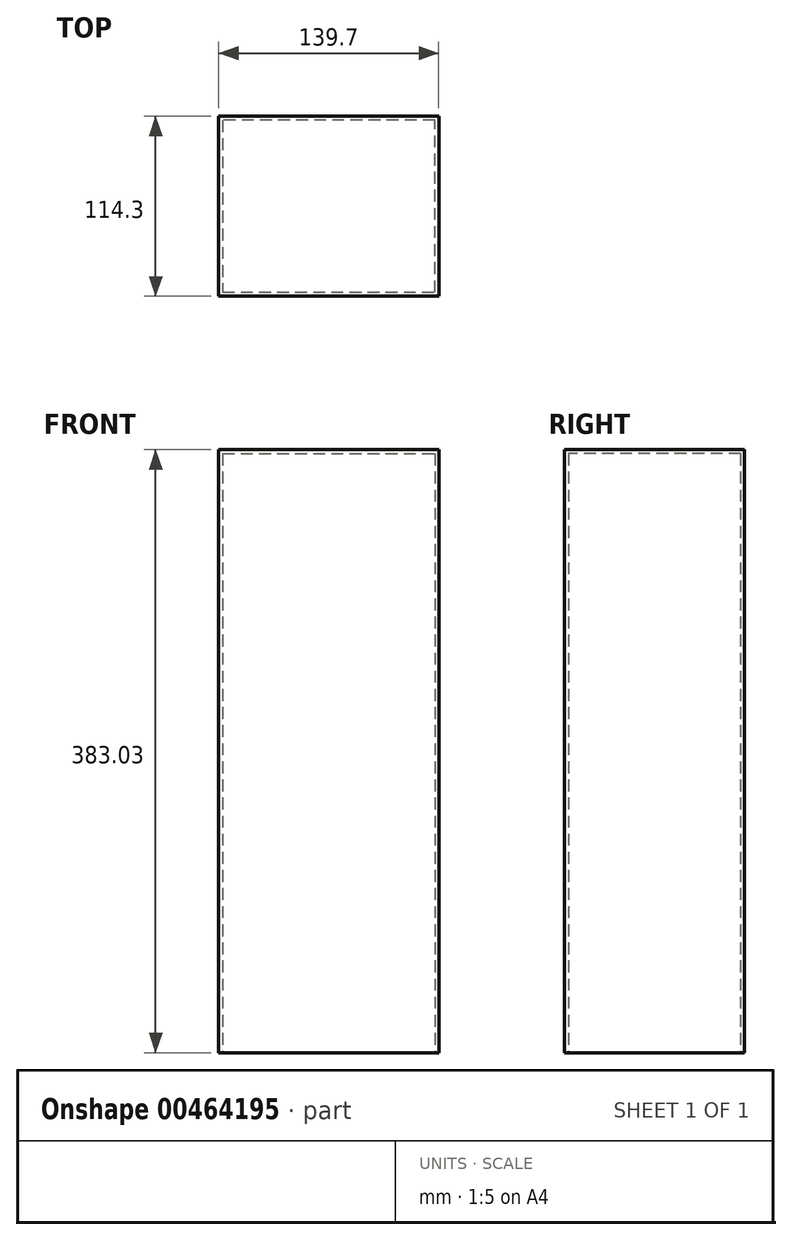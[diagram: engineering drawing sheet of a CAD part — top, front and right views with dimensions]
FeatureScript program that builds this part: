
annotation { "Feature Type Name" : "Feature", "Feature Type Description" : "" }
export const myFeature = defineFeature(function(context is Context, id is Id, definition is map)
    precondition{}
    {
        {
            var Q0;
            Q0=qCreatedBy(makeId("Top.planeOp"),FACE);
            var sketch = newSketch(context, id + "F0", { "sketchPlane" : qUnion([Q0])});
            skLineSegment(sketch, "E0", {"start": v(-63.05, -39.13) * mm, "end": v(76.65, -39.13) * mm});
            skLineSegment(sketch, "E1", {"start": v(76.65, -39.13) * mm, "end": v(76.65, 75.17) * mm});
            skLineSegment(sketch, "E2", {"start": v(76.65, 75.17) * mm, "end": v(-63.05, 75.17) * mm});
            skLineSegment(sketch, "E3", {"start": v(-63.05, 75.17) * mm, "end": v(-63.05, -39.13) * mm});
            skSolve(sketch);
        }
        {
            var Q0;
            Q0 = qSketchRegion(id + "F0", true);
            extrude(context, id + "F1", {"entities" : qUnion([Q0]), "depth" : 383.03 * mm});
        }
        {
            var Q0;
            Q0=makeQuery(id+"F1.opExtrude","CAP_FACE",FACE,{"disambiguationData":[OSD([sQuery(id+"F0.wireOp",EDGE,"E0"),sQuery(id+"F0.wireOp",EDGE,"E1"),sQuery(id+"F0.wireOp",EDGE,"E2"),sQuery(id+"F0.wireOp",EDGE,"E3")])],"isStart":true});
            shell(context, id + "F2", {"entities" : qUnion([Q0]), "thickness" : 2.54 * mm});
        }
    });
